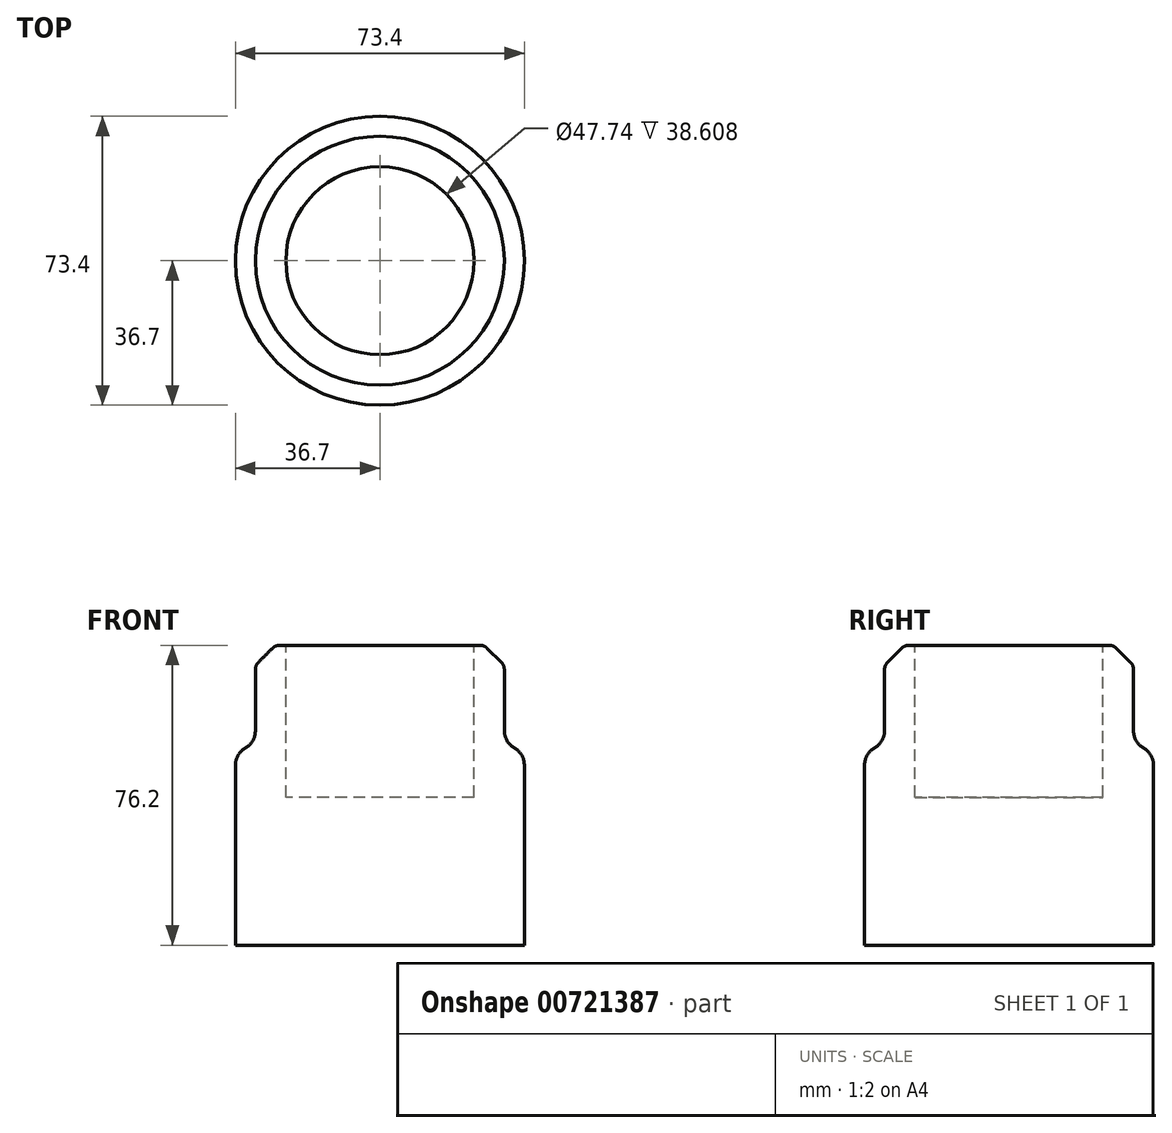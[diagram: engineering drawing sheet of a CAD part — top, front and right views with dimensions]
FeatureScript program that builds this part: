
annotation { "Feature Type Name" : "Feature", "Feature Type Description" : "" }
export const myFeature = defineFeature(function(context is Context, id is Id, definition is map)
    precondition{}
    {
        {
            var Q0;
            Q0=qCreatedBy(makeId("Top.planeOp"),FACE);
            var sketch = newSketch(context, id + "F0", { "sketchPlane" : qUnion([Q0])});
            skCircle(sketch, "E0", {"center": v(0, 0) * mm, "radius": 36.7 * mm});
            skSolve(sketch);
        }
        {
            var Q0;
            Q0=makeQuery(id+"F0.imprint","IMPRINT",FACE,{"disambiguationData":[TD([[makeQuery(id+"F0.imprint","IMPRINT",EDGE,{"derivedFrom":sQuery(id+"F0.wireOp",EDGE,"E0")}),1.0]])]});
            extrude(context, id + "F1", {"entities" : qUnion([Q0]), "depth" : 50.8 * mm, "offsetDistance" : 25.4 * mm});
        }
        {
            var Q0;
            Q0=makeQuery(id+"F1.opExtrude","CAP_EDGE",EDGE,{"disambiguationData":[OSD([sQuery(id+"F0.wireOp",EDGE,"E0")])],"isStart":false});
            fillet(context, id + "F2", {"entities" : qUnion([Q0]), "radius" : 5.08 * mm, "tangentPropagation" : true, "allowEdgeOverflow" : false});
        }
        {
            var Q0;
            Q0=makeQuery(id+"F1.opExtrude","CAP_FACE",FACE,{"disambiguationData":[OSD([sQuery(id+"F0.wireOp",EDGE,"E0")])],"isStart":false});
            var sketch = newSketch(context, id + "F3", { "sketchPlane" : qUnion([Q0])});
            skCircle(sketch, "E1", {"center": v(0, 0) * mm, "radius": 23.87 * mm});
            skSolve(sketch);
        }
        {
            var Q0;
            Q0=makeQuery(id+"F3.imprint","IMPRINT",FACE,{"disambiguationData":[TD([[makeQuery(id+"F3.imprint","IMPRINT",EDGE,{"derivedFrom":sQuery(id+"F3.wireOp",EDGE,"E1")}),1.0]])]});
            extrude(context, id + "F4", {"entities" : qUnion([Q0]), "operationType" : NewBodyOperationType.REMOVE, "oppositeDirection" : true, "depth" : 13.2 * mm, "offsetDistance" : 25.4 * mm});
        }
        {
            var Q0;
            Q0=makeQuery(id+"F1.opExtrude","CAP_FACE",FACE,{"disambiguationData":[OSD([sQuery(id+"F0.wireOp",EDGE,"E0")])],"isStart":false});
            extrude(context, id + "F5", {"entities" : qUnion([Q0]), "operationType" : NewBodyOperationType.ADD, "depth" : 25.4 * mm, "offsetDistance" : 25.4 * mm});
        }
        {
            var Q0;
            {var subQ0=sQuery(id+"F0.wireOp",EDGE,"E0");Q0=makeQuery(id+"F5.boolean.opBoolean","MERGE",EDGE,{"derivedFrom":[makeQuery(id+"F2.opFillet","BLEND_EDGE",EDGE,{"blendedFrom":[makeQuery(id+"F1.opExtrude","CAP_EDGE",EDGE,{"disambiguationData":[OSD([subQ0])],"isStart":false}),makeQuery(id+"F1.opExtrude","CAP_FACE",FACE,{"disambiguationData":[OSD([subQ0])],"isStart":false})],"blendedInto":[makeQuery(id+"F1.opExtrude","CAP_FACE",FACE,{"disambiguationData":[OSD([subQ0])],"isStart":false})]}),makeQuery(id+"F5.opExtrude","CAP_EDGE",EDGE,{"disambiguationData":[OSD([subQ0])],"isStart":true})]});}
            fillet(context, id + "F6", {"entities" : qUnion([Q0]), "radius" : 5.08 * mm, "tangentPropagation" : true, "allowEdgeOverflow" : false});
        }
        {
            var Q0;
            Q0=makeQuery(id+"F5.opExtrude","CAP_EDGE",EDGE,{"disambiguationData":[OSD([sQuery(id+"F0.wireOp",EDGE,"E0")])],"isStart":false});
            chamfer(context, id + "F7", {"entities" : qUnion([Q0]), "width" : 5.08 * mm, "tangentPropagation" : true});
        }
        {
            var Q0;
            {var subQ0=sQuery(id+"F0.wireOp",EDGE,"E0");Q0=makeQuery(id+"F7.opChamfer","BLEND_EDGE",EDGE,{"blendedFrom":[makeQuery(id+"F5.opExtrude","CAP_EDGE",EDGE,{"disambiguationData":[OSD([subQ0])],"isStart":false}),makeQuery(id+"F5.opExtrude","SWEPT_FACE",FACE,{"disambiguationData":[OSD([subQ0])]})],"blendedInto":[makeQuery(id+"F5.opExtrude","SWEPT_FACE",FACE,{"disambiguationData":[OSD([subQ0])]})]});}
            fillet(context, id + "F8", {"entities" : qUnion([Q0]), "radius" : 2.54 * mm, "tangentPropagation" : true, "allowEdgeOverflow" : false});
        }
        {
            var Q0;
            {var subQ0=sQuery(id+"F0.wireOp",EDGE,"E0");Q0=makeQuery(id+"F7.opChamfer","BLEND_EDGE",EDGE,{"blendedFrom":[makeQuery(id+"F5.opExtrude","CAP_EDGE",EDGE,{"disambiguationData":[OSD([subQ0])],"isStart":false}),makeQuery(id+"F5.opExtrude","CAP_FACE",FACE,{"disambiguationData":[OSD([subQ0])],"isStart":false})],"blendedInto":[makeQuery(id+"F5.opExtrude","CAP_FACE",FACE,{"disambiguationData":[OSD([subQ0])],"isStart":false})]});}
            fillet(context, id + "F9", {"entities" : qUnion([Q0]), "radius" : 2.54 * mm, "tangentPropagation" : true, "allowEdgeOverflow" : false});
        }
    });
